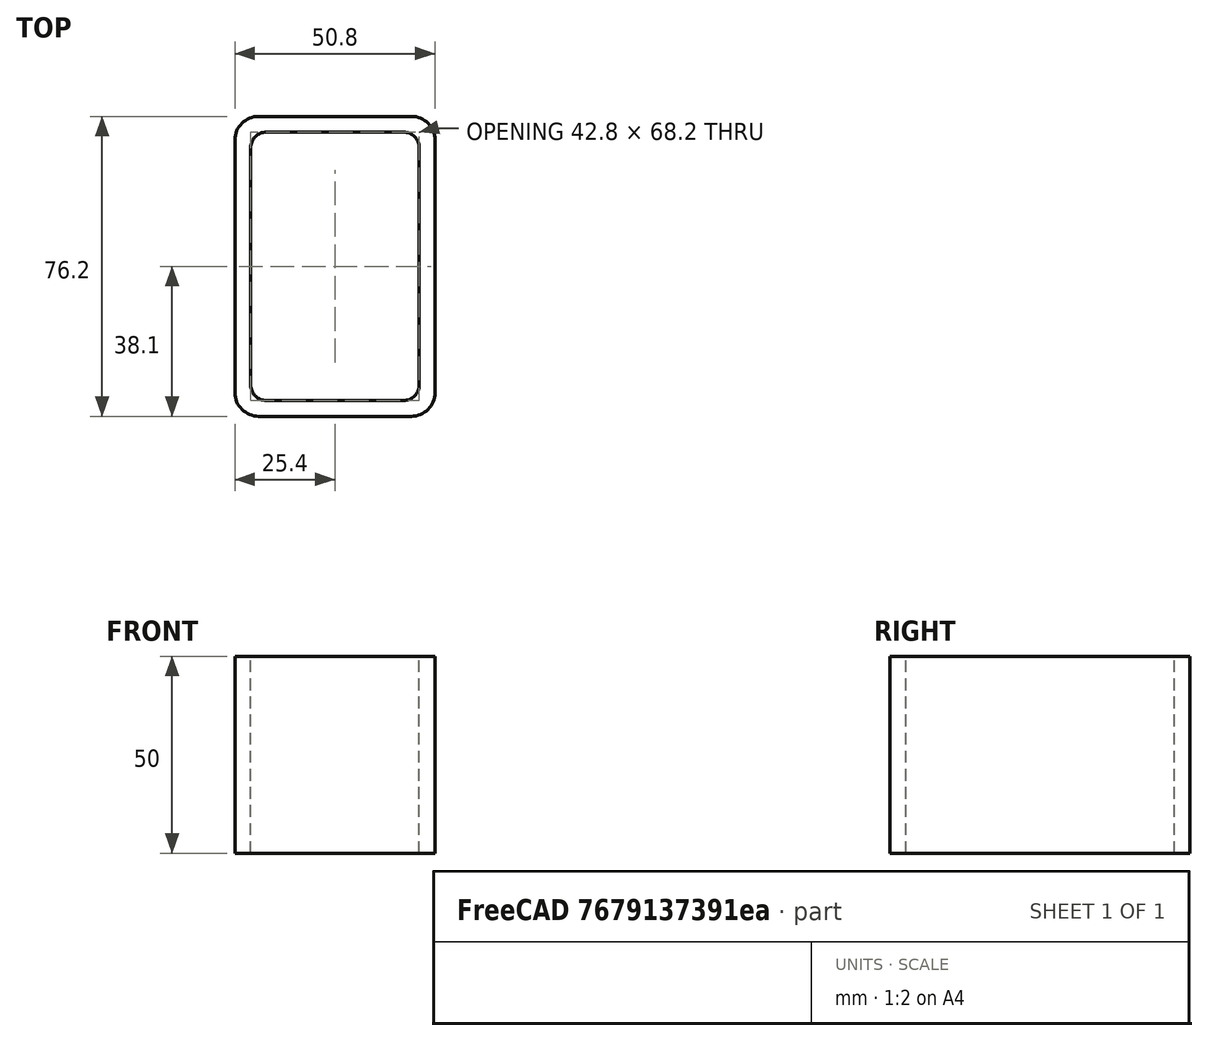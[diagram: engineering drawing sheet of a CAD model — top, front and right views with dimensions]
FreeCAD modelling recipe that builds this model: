
FCSTD DOCUMENT  (FreeCAD 0.15R4671 (Git))
Label: Rectangular hollow section 76.2 x50.8 x4 EN10219 S235JRH
License: All rights reserved
LicenseURL: http://en.wikipedia.org/wiki/All_rights_reserved
objects: Sketcher::SketchObject×1, Part::Extrusion×1
note: 2 computed .brp shape members not serialized (recipe doc carries the construction recipe); baked Part::Feature solids carry a one-line shape summary decoded from their .brp

FEATURE [Sketcher::SketchObject] Sketch
  sketch-geometry (16):
    g0: LineSegment StartX=-17.4 StartY=34.1 StartZ=0 EndX=17.4 EndY=34.1 EndZ=0
    g1: LineSegment StartX=21.4 StartY=30.1 StartZ=0 EndX=21.4 EndY=-30.1 EndZ=0
    g2: LineSegment StartX=17.4 StartY=-34.1 StartZ=0 EndX=-17.4 EndY=-34.1 EndZ=0
    g3: LineSegment StartX=-21.4 StartY=-30.1 StartZ=0 EndX=-21.4 EndY=30.1 EndZ=0
    g4: LineSegment StartX=-19.4 StartY=38.1 StartZ=0 EndX=19.4 EndY=38.1 EndZ=0
    g5: LineSegment StartX=25.4 StartY=32.1 StartZ=0 EndX=25.4 EndY=-32.1 EndZ=0
    g6: LineSegment StartX=19.4 StartY=-38.1 StartZ=0 EndX=-19.4 EndY=-38.1 EndZ=0
    g7: LineSegment StartX=-25.4 StartY=-32.1 StartZ=0 EndX=-25.4 EndY=32.1 EndZ=0
    g8: ArcOfCircle CenterX=-17.4 CenterY=30.1 CenterZ=0 NormalX=0 NormalY=0 NormalZ=1 Radius=4 StartAngle=1.5708 EndAngle=3.14159
    g9: ArcOfCircle CenterX=17.4 CenterY=30.1 CenterZ=0 NormalX=0 NormalY=0 NormalZ=1 Radius=4 StartAngle=0 EndAngle=1.5708
    g10: ArcOfCircle CenterX=17.4 CenterY=-30.1 CenterZ=0 NormalX=0 NormalY=0 NormalZ=1 Radius=4 StartAngle=4.71239 EndAngle=6.28319
    g11: ArcOfCircle CenterX=-17.4 CenterY=-30.1 CenterZ=0 NormalX=0 NormalY=0 NormalZ=1 Radius=4 StartAngle=3.14159 EndAngle=4.71239
    g12: ArcOfCircle CenterX=19.4 CenterY=32.1 CenterZ=0 NormalX=0 NormalY=0 NormalZ=1 Radius=6 StartAngle=0 EndAngle=1.5708
    g13: ArcOfCircle CenterX=19.4 CenterY=-32.1 CenterZ=0 NormalX=0 NormalY=0 NormalZ=1 Radius=6 StartAngle=4.71239 EndAngle=6.28319
    g14: ArcOfCircle CenterX=-19.4 CenterY=-32.1 CenterZ=0 NormalX=0 NormalY=0 NormalZ=1 Radius=6 StartAngle=3.14159 EndAngle=4.71239
    g15: ArcOfCircle CenterX=-19.4 CenterY=32.1 CenterZ=0 NormalX=0 NormalY=0 NormalZ=1 Radius=6 StartAngle=1.5708 EndAngle=3.14159
  constraints (36):
    c: Horizontal(g2)
    c: Vertical(g3)
    c: Horizontal(g6)
    c: Vertical(g7)
    c: Tangent(g3,g8) = 1.5708
    c: Tangent(g0,g8) = 1.5708
    c: Tangent(g0,g9) = 1.5708
    c: Tangent(g1,g9) = 1.5708
    c: Tangent(g1,g10) = 1.5708
    c: Tangent(g2,g10) = 1.5708
    c: Tangent(g2,g11) = 1.5708
    c: Tangent(g3,g11) = 1.5708
    c: Tangent(g4,g12) = 1.5708
    c: Tangent(g5,g12) = 1.5708
    c: Tangent(g5,g13) = 1.5708
    c: Tangent(g6,g13) = 1.5708
    c: Tangent(g6,g14) = 1.5708
    c: Tangent(g7,g14) = 1.5708
    c: Tangent(g7,g15) = 1.5708
    c: Tangent(g4,g15) = 1.5708
    c: Equal(g9,g8)
    c: Equal(g9,g11)
    c: Equal(g9,g10)
    c: Equal(g12,g15)
    c: Equal(g12,g14)
    c: Equal(g12,g13)
    c: Symmetric(g4,g6,g-1)
    c: Symmetric(g7,g5,g-2)
    c: DistanceY(g4,g6) = -76.2
    c: DistanceX(g7,g5) = 50.8
    c: Symmetric(g3,g1,g-2)
    c: Symmetric(g0,g2,g-1)
    c: DistanceY(g0,g4) = 4
    c: DistanceX(g5,g1) = -4
    c: Radius(g9) = 4
    c: Radius(g12) = 6
FEATURE [Part::Extrusion] Extrude  label="Rectangular hollow section 76.2 x50.8 x4 EN10219 S235JRH"
  Base = -> Sketch
  Dir = (0,0,50)
  Solid = true
